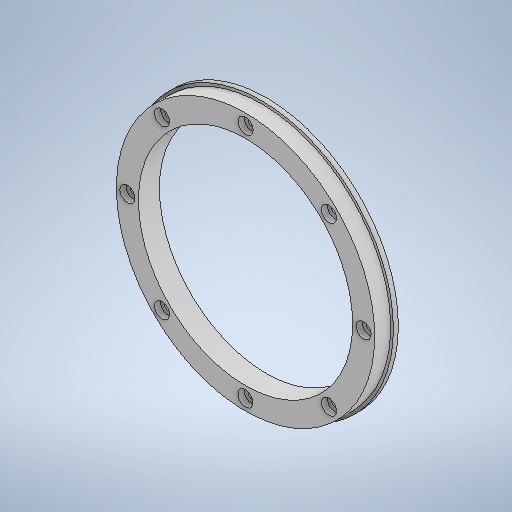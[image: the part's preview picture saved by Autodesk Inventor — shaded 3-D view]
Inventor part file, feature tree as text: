
AUTODESK INVENTOR PART (.ipt)
format: ipt  version: 2025 (Build 290162010, 162A)  size: 327,168 bytes
history: native  units: mm
features: extrude x4, sketch x4, pattern_circular x1, projected_geometry x1
ambient origin geometry x8: Origin, YZ Plane, XZ Plane, XY Plane, X Axis, Y Axis, Z Axis, Center Point
bodies: Solid1 (feature_tree)
feature tree (10):
  extrude  "Extrusion1"  Depth=389.0mm
  extrude  "Extrusion2"  Depth=38.0mm
  extrude  "Extrusion3"  Depth=80.0mm TaperAngle=360.0deg
  pattern_circular  "Circular Pattern1"  [2 undecoded]
  extrude  "Extrusion4"  Depth=9.0mm
  sketch  "Sketch1"  dims[d0=40.0mm d1=389.0mm]
  sketch  "Sketch2"  dims[d2=38.0mm d3=0.0mm d4=12.5mm]
  projected_geometry  "Projected Loop1"
  sketch  "Sketch3"  dims[d5=0.0mm d6=0.0mm d7=80.0mm d8=360.0deg]
  sketch  "Sketch4"  dims[d10=27.5mm d11=11.0mm d12=0.0mm d13=5.0mm d14=9.0mm d15=0.0mm]
note: 2 required parameter values undecoded (feature->parameter linkage not recoverable at this tier; creation-order binding heuristic only, values carry confidence <= 0.55)
